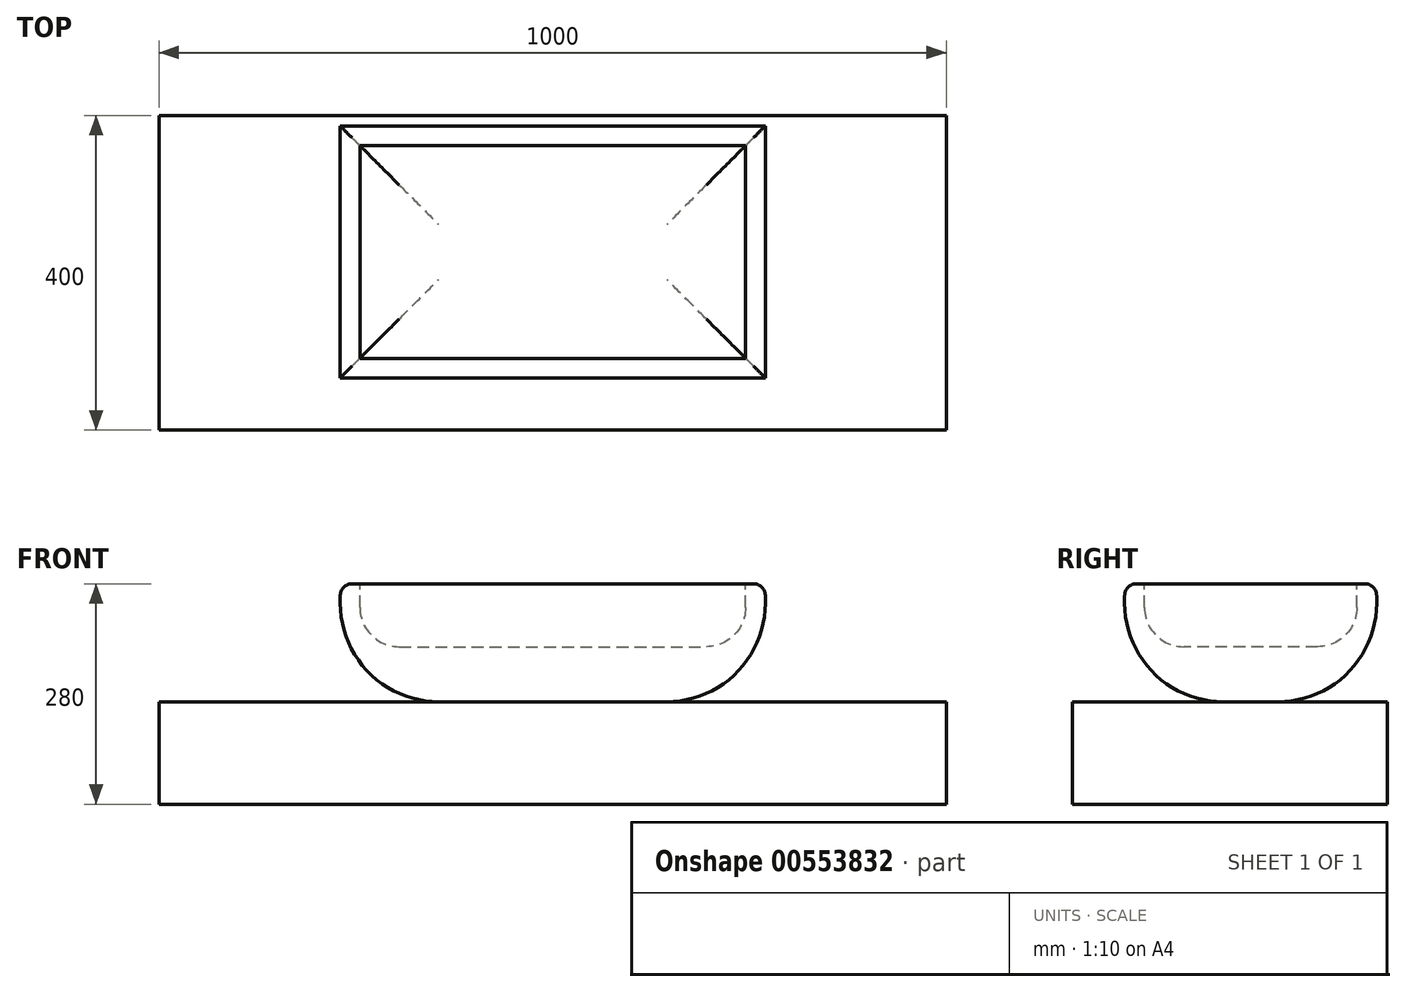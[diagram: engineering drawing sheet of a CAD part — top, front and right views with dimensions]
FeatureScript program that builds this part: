
annotation { "Feature Type Name" : "Feature", "Feature Type Description" : "" }
export const myFeature = defineFeature(function(context is Context, id is Id, definition is map)
    precondition{}
    {
        {
            var Q0;
            Q0=qCreatedBy(makeId("Top.planeOp"),FACE);
            var sketch = newSketch(context, id + "F0", { "sketchPlane" : qUnion([Q0])});
            skLineSegment(sketch, "E0.bottom", {"start": v(-505.84, 138.3) * mm, "end": v(494.16, 138.3) * mm});
            skLineSegment(sketch, "E0.top", {"start": v(-505.84, -261.7) * mm, "end": v(494.16, -261.7) * mm});
            skLineSegment(sketch, "E0.left", {"start": v(-505.84, 138.3) * mm, "end": v(-505.84, -261.7) * mm});
            skLineSegment(sketch, "E0.right", {"start": v(494.16, 138.3) * mm, "end": v(494.16, -261.7) * mm});
            skSolve(sketch);
        }
        {
            var Q0;
            Q0=makeQuery(id+"F0.imprint","IMPRINT",FACE,{"disambiguationData":[TD([[makeQuery(id+"F0.imprint","IMPRINT",EDGE,{"derivedFrom":sQuery(id+"F0.wireOp",EDGE,"E0.bottom")}),-1.0]])]});
            extrude(context, id + "F1", {"entities" : qUnion([Q0]), "depth" : 130 * mm, "offsetDistance" : 25 * mm});
        }
        {
            var Q0;
            Q0=makeQuery(id+"F1.opExtrude","CAP_FACE",FACE,{"disambiguationData":[OSD([sQuery(id+"F0.wireOp",EDGE,"E0.bottom"),sQuery(id+"F0.wireOp",EDGE,"E0.top"),sQuery(id+"F0.wireOp",EDGE,"E0.left"),sQuery(id+"F0.wireOp",EDGE,"E0.right")])],"isStart":false});
            cPlane(context, id + "F2", {"entities" : qUnion([Q0]), "cplaneType" : CPlaneType.OFFSET, "offset" : 0 * mm, "width" : 150 * mm, "height" : 150 * mm});
        }
        {
            var Q0;
            Q0=qCreatedBy(id+"F2.planeOp",FACE);
            var sketch = newSketch(context, id + "F3", { "sketchPlane" : qUnion([Q0])});
            skLineSegment(sketch, "E1.bottom", {"start": v(-275.84, 124.85) * mm, "end": v(264.16, 124.85) * mm});
            skLineSegment(sketch, "E1.top", {"start": v(-275.84, -195.27) * mm, "end": v(264.16, -195.27) * mm});
            skLineSegment(sketch, "E1.left", {"start": v(-275.84, 124.85) * mm, "end": v(-275.84, -195.27) * mm});
            skLineSegment(sketch, "E1.right", {"start": v(264.16, 124.85) * mm, "end": v(264.16, -195.27) * mm});
            skSolve(sketch);
        }
        {
            var Q0;
            Q0=makeQuery(id+"F3.imprint","IMPRINT",FACE,{"disambiguationData":[TD([[makeQuery(id+"F3.imprint","IMPRINT",EDGE,{"derivedFrom":sQuery(id+"F3.wireOp",EDGE,"E1.bottom")}),-1.0]])]});
            extrude(context, id + "F4", {"entities" : qUnion([Q0]), "depth" : 150 * mm, "offsetDistance" : 25 * mm});
        }
        {
            var Q0;
            Q0=makeQuery(id+"F4.opExtrude","CAP_EDGE",EDGE,{"disambiguationData":[OSD([sQuery(id+"F3.wireOp",EDGE,"E1.top")])],"isStart":true});
            var Q1;
            Q1=makeQuery(id+"F4.opExtrude","CAP_EDGE",EDGE,{"disambiguationData":[OSD([sQuery(id+"F3.wireOp",EDGE,"E1.right")])],"isStart":true});
            var Q2;
            Q2=makeQuery(id+"F4.opExtrude","CAP_EDGE",EDGE,{"disambiguationData":[OSD([sQuery(id+"F3.wireOp",EDGE,"E1.bottom")])],"isStart":true});
            var Q3;
            Q3=makeQuery(id+"F4.opExtrude","CAP_EDGE",EDGE,{"disambiguationData":[OSD([sQuery(id+"F3.wireOp",EDGE,"E1.left")])],"isStart":true});
            fillet(context, id + "F5", {"entities" : qUnion([Q0, Q1, Q2, Q3]), "radius" : 125 * mm, "tangentPropagation" : true, "allowEdgeOverflow" : false});
        }
        {
            var Q0;
            Q0=makeQuery(id+"F4.opExtrude","CAP_EDGE",EDGE,{"disambiguationData":[OSD([sQuery(id+"F3.wireOp",EDGE,"E1.top")])],"isStart":false});
            var Q1;
            Q1=makeQuery(id+"F4.opExtrude","CAP_EDGE",EDGE,{"disambiguationData":[OSD([sQuery(id+"F3.wireOp",EDGE,"E1.left")])],"isStart":false});
            var Q2;
            Q2=makeQuery(id+"F4.opExtrude","CAP_EDGE",EDGE,{"disambiguationData":[OSD([sQuery(id+"F3.wireOp",EDGE,"E1.bottom")])],"isStart":false});
            var Q3;
            Q3=makeQuery(id+"F4.opExtrude","CAP_EDGE",EDGE,{"disambiguationData":[OSD([sQuery(id+"F3.wireOp",EDGE,"E1.right")])],"isStart":false});
            fillet(context, id + "F6", {"entities" : qUnion([Q0, Q1, Q2, Q3]), "radius" : 15 * mm, "tangentPropagation" : true, "allowEdgeOverflow" : false});
        }
        {
            var Q0;
            Q0=makeQuery(id+"F4.opExtrude","CAP_FACE",FACE,{"disambiguationData":[OSD([sQuery(id+"F3.wireOp",EDGE,"E1.bottom"),sQuery(id+"F3.wireOp",EDGE,"E1.top"),sQuery(id+"F3.wireOp",EDGE,"E1.left"),sQuery(id+"F3.wireOp",EDGE,"E1.right")])],"isStart":false});
            var sketch = newSketch(context, id + "F7", { "sketchPlane" : qUnion([Q0])});
            skLineSegment(sketch, "E2.bottom", {"start": v(-250.84, 99.85) * mm, "end": v(239.16, 99.85) * mm});
            skLineSegment(sketch, "E2.top", {"start": v(-250.84, -170.27) * mm, "end": v(239.16, -170.27) * mm});
            skLineSegment(sketch, "E2.left", {"start": v(-250.84, 99.85) * mm, "end": v(-250.84, -170.27) * mm});
            skLineSegment(sketch, "E2.right", {"start": v(239.16, 99.85) * mm, "end": v(239.16, -170.27) * mm});
            skSolve(sketch);
        }
        {
            var Q0;
            Q0=makeQuery(id+"F7.imprint","IMPRINT",FACE,{"disambiguationData":[TD([[makeQuery(id+"F7.imprint","IMPRINT",EDGE,{"derivedFrom":sQuery(id+"F7.wireOp",EDGE,"E2.bottom")}),-1.0]])]});
            extrude(context, id + "F8", {"entities" : qUnion([Q0]), "operationType" : NewBodyOperationType.REMOVE, "oppositeDirection" : true, "depth" : 80 * mm, "offsetDistance" : 25 * mm});
        }
        {
            var Q0;
            Q0=makeQuery(id+"F8.boolean.opBoolean","COPY",EDGE,{"derivedFrom":makeQuery(id+"F8.opExtrude","CAP_EDGE",EDGE,{"disambiguationData":[OSD([sQuery(id+"F7.wireOp",EDGE,"E2.bottom")])],"isStart":false})});
            var Q1;
            Q1=makeQuery(id+"F8.boolean.opBoolean","COPY",EDGE,{"derivedFrom":makeQuery(id+"F8.opExtrude","CAP_EDGE",EDGE,{"disambiguationData":[OSD([sQuery(id+"F7.wireOp",EDGE,"E2.left")])],"isStart":false})});
            var Q2;
            Q2=makeQuery(id+"F8.boolean.opBoolean","COPY",EDGE,{"derivedFrom":makeQuery(id+"F8.opExtrude","CAP_EDGE",EDGE,{"disambiguationData":[OSD([sQuery(id+"F7.wireOp",EDGE,"E2.right")])],"isStart":false})});
            var Q3;
            Q3=makeQuery(id+"F8.boolean.opBoolean","COPY",EDGE,{"derivedFrom":makeQuery(id+"F8.opExtrude","CAP_EDGE",EDGE,{"disambiguationData":[OSD([sQuery(id+"F7.wireOp",EDGE,"E2.top")])],"isStart":false})});
            fillet(context, id + "F9", {"entities" : qUnion([Q0, Q1, Q2, Q3]), "radius" : 50 * mm, "tangentPropagation" : true, "allowEdgeOverflow" : false});
        }
    });
